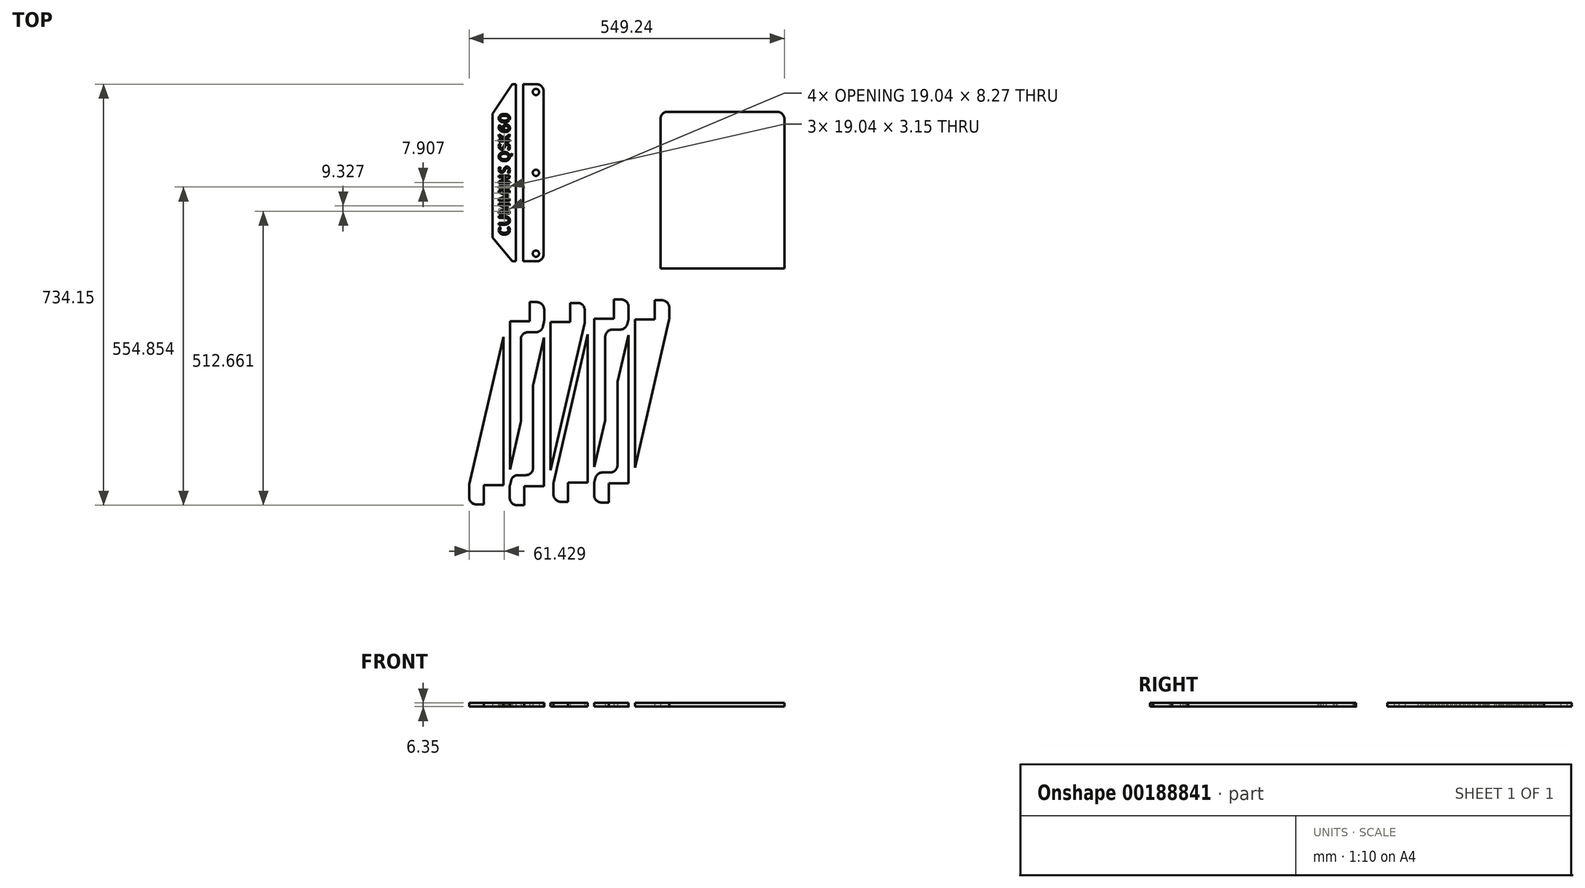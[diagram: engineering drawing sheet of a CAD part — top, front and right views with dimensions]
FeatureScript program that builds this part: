
annotation { "Feature Type Name" : "Feature", "Feature Type Description" : "" }
export const myFeature = defineFeature(function(context is Context, id is Id, definition is map)
    precondition{}
    {
        {
            var Q0;
            Q0=qCreatedBy(makeId("Top.planeOp"),FACE);
            var sketch = newSketch(context, id + "F0", { "sketchPlane" : qUnion([Q0])});
            skLineSegment(sketch, "E0.bottom", {"start": v(22.12, 104.51) * mm, "end": v(238.02, 104.51) * mm});
            skLineSegment(sketch, "E0.top", {"start": v(34.82, 377.56) * mm, "end": v(225.32, 377.56) * mm});
            skLineSegment(sketch, "E0.left", {"start": v(22.12, 104.51) * mm, "end": v(22.12, 364.86) * mm});
            skLineSegment(sketch, "E0.right", {"start": v(238.02, 104.51) * mm, "end": v(238.02, 364.86) * mm});
            skPoint(sketch, "E1.visualSharp", {"position": v(22.12, 377.56) * mm});
            skArc(sketch, "E1.filletArc", {"start": v(34.82, 377.56) * mm, "mid": v(25.83, 373.84) * mm, "end": v(22.12, 364.86) * mm});
            skPoint(sketch, "E2.visualSharp", {"position": v(238.02, 377.56) * mm});
            skArc(sketch, "E2.filletArc", {"start": v(238.02, 364.86) * mm, "mid": v(234.3, 373.84) * mm, "end": v(225.32, 377.56) * mm});
            skPoint(sketch, "E3", {"position": v(-194.8, 412.07) * mm});
            skPoint(sketch, "E4", {"position": v(-194.8, 271.07) * mm});
            skPoint(sketch, "E5", {"position": v(-194.8, 130.08) * mm});
            skLineSegment(sketch, "E6", {"start": v(-181.3, 129.3) * mm, "end": v(-181.3, 412.86) * mm});
            skLineSegment(sketch, "E7", {"start": v(-194, 116.6) * mm, "end": v(-216.87, 116.6) * mm});
            skLineSegment(sketch, "E8", {"start": v(-194, 425.56) * mm, "end": v(-216.87, 425.56) * mm});
            skPoint(sketch, "E9.visualSharp", {"position": v(-181.3, 116.6) * mm});
            skArc(sketch, "E9.filletArc", {"start": v(-194, 116.6) * mm, "mid": v(-185.03, 120.31) * mm, "end": v(-181.3, 129.3) * mm});
            skPoint(sketch, "E10.visualSharp", {"position": v(-181.3, 425.56) * mm});
            skArc(sketch, "E10.filletArc", {"start": v(-181.3, 412.86) * mm, "mid": v(-185.03, 421.84) * mm, "end": v(-194, 425.56) * mm});
            skLineSegment(sketch, "E11", {"start": v(-216.87, 116.6) * mm, "end": v(-216.87, 425.56) * mm});
            skLineSegment(sketch, "E12", {"start": v(-270.11, 158.02) * mm, "end": v(-270.11, 373.97) * mm});
            skLineSegment(sketch, "E13", {"start": v(-270.11, 373.97) * mm, "end": v(-235.82, 425.56) * mm});
            skLineSegment(sketch, "E14", {"start": v(-235.82, 425.56) * mm, "end": v(-229.47, 425.56) * mm});
            skLineSegment(sketch, "E15", {"start": v(-229.47, 425.56) * mm, "end": v(-229.47, 116.6) * mm});
            skLineSegment(sketch, "E16", {"start": v(-229.47, 116.6) * mm, "end": v(-235.82, 116.6) * mm});
            skLineSegment(sketch, "E17", {"start": v(-235.82, 116.6) * mm, "end": v(-270.11, 158.02) * mm});
            skText(sketch, "E18", { "text": "CUMMINS QSK60", "fontName": "AllertaStencil-Regular.ttf"});
            skLineSegment(sketch, "E19", {"start": v(-169.38, -247.72) * mm, "end": v(-110.01, 9.41) * mm});
            skLineSegment(sketch, "E20", {"start": v(-109.69, 12.27) * mm, "end": v(-109.69, 31.47) * mm});
            skLineSegment(sketch, "E21", {"start": v(-122.39, 44.17) * mm, "end": v(-135.09, 44.17) * mm});
            skLineSegment(sketch, "E22", {"start": v(-135.09, 44.17) * mm, "end": v(-135.09, 10.82) * mm});
            skLineSegment(sketch, "E23", {"start": v(-135.09, 10.82) * mm, "end": v(-169.38, 10.82) * mm});
            skLineSegment(sketch, "E24", {"start": v(-169.38, 10.82) * mm, "end": v(-169.38, -247.72) * mm});
            skPoint(sketch, "E25.visualSharp", {"position": v(-109.69, 44.17) * mm});
            skArc(sketch, "E25.filletArc", {"start": v(-109.69, 31.47) * mm, "mid": v(-113.4, 40.45) * mm, "end": v(-122.39, 44.17) * mm});
            skLineSegment(sketch, "E26", {"start": v(-180.48, 13.57) * mm, "end": v(-180.48, 32.77) * mm});
            skLineSegment(sketch, "E27", {"start": v(-193.18, 45.47) * mm, "end": v(-205.88, 45.47) * mm});
            skLineSegment(sketch, "E28", {"start": v(-205.88, 45.47) * mm, "end": v(-205.88, 12.12) * mm});
            skLineSegment(sketch, "E29", {"start": v(-205.88, 12.12) * mm, "end": v(-240.17, 12.12) * mm});
            skLineSegment(sketch, "E30", {"start": v(-240.17, 12.12) * mm, "end": v(-240.17, -246.42) * mm});
            skPoint(sketch, "E31.visualSharp", {"position": v(-180.48, 45.47) * mm});
            skArc(sketch, "E31.filletArc", {"start": v(-180.48, 32.77) * mm, "mid": v(-184.2, 41.75) * mm, "end": v(-193.18, 45.47) * mm});
            skPoint(sketch, "E32.visualSharp", {"position": v(-180.48, 12.12) * mm});
            skArc(sketch, "E32.filletArc", {"start": v(-180.8, 10.71) * mm, "mid": v(-180.56, 12.13) * mm, "end": v(-180.48, 13.57) * mm});
            skPoint(sketch, "E33.visualSharp", {"position": v(-109.69, 10.82) * mm});
            skArc(sketch, "E33.filletArc", {"start": v(-110.01, 9.41) * mm, "mid": v(-109.77, 10.83) * mm, "end": v(-109.69, 12.27) * mm});
            skLineSegment(sketch, "E34", {"start": v(-221.12, -19.63) * mm, "end": v(-221.12, -162.46) * mm});
            skLineSegment(sketch, "E35", {"start": v(-208.42, -6.93) * mm, "end": v(-194.98, -6.93) * mm});
            skLineSegment(sketch, "E36", {"start": v(-240.17, -246.42) * mm, "end": v(-221.45, -165.32) * mm});
            skLineSegment(sketch, "E37", {"start": v(-182.6, 2.92) * mm, "end": v(-180.8, 10.71) * mm});
            skPoint(sketch, "E38.visualSharp", {"position": v(-221.12, -163.9) * mm});
            skArc(sketch, "E38.filletArc", {"start": v(-221.45, -165.32) * mm, "mid": v(-221.2, -163.9) * mm, "end": v(-221.12, -162.46) * mm});
            skPoint(sketch, "E39.visualSharp", {"position": v(-184.88, -6.93) * mm});
            skArc(sketch, "E39.filletArc", {"start": v(-194.98, -6.93) * mm, "mid": v(-187.07, -4.16) * mm, "end": v(-182.6, 2.92) * mm});
            skPoint(sketch, "E40.visualSharp", {"position": v(-221.12, -6.93) * mm});
            skArc(sketch, "E40.filletArc", {"start": v(-208.42, -6.93) * mm, "mid": v(-217.4, -10.65) * mm, "end": v(-221.12, -19.63) * mm});
            skCircle(sketch, "E41", {"center": v(-194.8, 130.08) * mm, "radius": 5.5 * mm});
            skCircle(sketch, "E42", {"center": v(-194.8, 271.07) * mm, "radius": 5.5 * mm});
            skCircle(sketch, "E43", {"center": v(-194.8, 412.07) * mm, "radius": 5.5 * mm});
            skLineSegment(sketch, "E44", {"start": v(-22.32, -243.1) * mm, "end": v(37.04, 14.03) * mm});
            skLineSegment(sketch, "E45", {"start": v(37.37, 16.89) * mm, "end": v(37.37, 36.09) * mm});
            skLineSegment(sketch, "E46", {"start": v(24.67, 48.79) * mm, "end": v(11.97, 48.79) * mm});
            skLineSegment(sketch, "E47", {"start": v(11.97, 48.79) * mm, "end": v(11.97, 15.44) * mm});
            skLineSegment(sketch, "E48", {"start": v(11.97, 15.44) * mm, "end": v(-22.32, 15.44) * mm});
            skLineSegment(sketch, "E49", {"start": v(-22.32, 15.44) * mm, "end": v(-22.32, -243.1) * mm});
            skPoint(sketch, "E50.visualSharp", {"position": v(37.37, 48.79) * mm});
            skArc(sketch, "E50.filletArc", {"start": v(37.37, 36.09) * mm, "mid": v(33.65, 45.07) * mm, "end": v(24.67, 48.79) * mm});
            skLineSegment(sketch, "E51", {"start": v(-33.42, 18.19) * mm, "end": v(-33.42, 37.39) * mm});
            skLineSegment(sketch, "E52", {"start": v(-46.12, 50.09) * mm, "end": v(-58.82, 50.09) * mm});
            skLineSegment(sketch, "E53", {"start": v(-58.82, 50.09) * mm, "end": v(-58.82, 16.74) * mm});
            skLineSegment(sketch, "E54", {"start": v(-58.82, 16.74) * mm, "end": v(-93.11, 16.74) * mm});
            skLineSegment(sketch, "E55", {"start": v(-93.11, 16.74) * mm, "end": v(-93.11, -241.8) * mm});
            skPoint(sketch, "E56.visualSharp", {"position": v(-33.42, 50.09) * mm});
            skArc(sketch, "E56.filletArc", {"start": v(-33.42, 37.39) * mm, "mid": v(-37.14, 46.37) * mm, "end": v(-46.12, 50.09) * mm});
            skPoint(sketch, "E57.visualSharp", {"position": v(-33.42, 16.74) * mm});
            skArc(sketch, "E57.filletArc", {"start": v(-33.75, 15.33) * mm, "mid": v(-33.5, 16.75) * mm, "end": v(-33.42, 18.19) * mm});
            skPoint(sketch, "E58.visualSharp", {"position": v(37.37, 15.44) * mm});
            skArc(sketch, "E58.filletArc", {"start": v(37.04, 14.03) * mm, "mid": v(37.29, 15.45) * mm, "end": v(37.37, 16.89) * mm});
            skLineSegment(sketch, "E59", {"start": v(-74.06, -15.01) * mm, "end": v(-74.06, -157.84) * mm});
            skLineSegment(sketch, "E60", {"start": v(-61.36, -2.31) * mm, "end": v(-47.92, -2.31) * mm});
            skLineSegment(sketch, "E61", {"start": v(-93.11, -241.8) * mm, "end": v(-74.39, -160.7) * mm});
            skLineSegment(sketch, "E62", {"start": v(-35.55, 7.53) * mm, "end": v(-33.75, 15.33) * mm});
            skPoint(sketch, "E63.visualSharp", {"position": v(-74.06, -159.3) * mm});
            skArc(sketch, "E63.filletArc", {"start": v(-74.39, -160.7) * mm, "mid": v(-74.15, -159.28) * mm, "end": v(-74.06, -157.84) * mm});
            skPoint(sketch, "E64.visualSharp", {"position": v(-37.82, -2.31) * mm});
            skArc(sketch, "E64.filletArc", {"start": v(-47.92, -2.31) * mm, "mid": v(-40.02, 0.45) * mm, "end": v(-35.55, 7.53) * mm});
            skPoint(sketch, "E65.visualSharp", {"position": v(-74.06, -2.31) * mm});
            skArc(sketch, "E65.filletArc", {"start": v(-61.36, -2.31) * mm, "mid": v(-70.34, -6.03) * mm, "end": v(-74.06, -15.01) * mm});
            skLineSegment(sketch, "E66", {"start": v(-104.48, -10.78) * mm, "end": v(-163.84, -267.92) * mm});
            skLineSegment(sketch, "E67", {"start": v(-164.17, -270.77) * mm, "end": v(-164.17, -289.98) * mm});
            skLineSegment(sketch, "E68", {"start": v(-151.47, -302.68) * mm, "end": v(-138.77, -302.68) * mm});
            skLineSegment(sketch, "E69", {"start": v(-138.77, -302.68) * mm, "end": v(-138.77, -269.33) * mm});
            skLineSegment(sketch, "E70", {"start": v(-138.77, -269.33) * mm, "end": v(-104.48, -269.33) * mm});
            skLineSegment(sketch, "E71", {"start": v(-104.48, -269.33) * mm, "end": v(-104.48, -10.78) * mm});
            skPoint(sketch, "E72.visualSharp", {"position": v(-164.17, -302.68) * mm});
            skArc(sketch, "E72.filletArc", {"start": v(-164.17, -289.98) * mm, "mid": v(-160.45, -298.96) * mm, "end": v(-151.47, -302.68) * mm});
            skLineSegment(sketch, "E73", {"start": v(-93.38, -272.07) * mm, "end": v(-93.38, -291.28) * mm});
            skLineSegment(sketch, "E74", {"start": v(-80.68, -303.98) * mm, "end": v(-67.98, -303.98) * mm});
            skLineSegment(sketch, "E75", {"start": v(-67.98, -303.98) * mm, "end": v(-67.98, -270.63) * mm});
            skLineSegment(sketch, "E76", {"start": v(-67.98, -270.63) * mm, "end": v(-33.69, -270.63) * mm});
            skLineSegment(sketch, "E77", {"start": v(-33.69, -270.63) * mm, "end": v(-33.69, -12.08) * mm});
            skPoint(sketch, "E78.visualSharp", {"position": v(-93.38, -303.98) * mm});
            skArc(sketch, "E78.filletArc", {"start": v(-93.38, -291.28) * mm, "mid": v(-89.66, -300.26) * mm, "end": v(-80.68, -303.98) * mm});
            skPoint(sketch, "E79.visualSharp", {"position": v(-93.38, -270.63) * mm});
            skArc(sketch, "E79.filletArc", {"start": v(-93.05, -269.22) * mm, "mid": v(-93.3, -270.64) * mm, "end": v(-93.38, -272.07) * mm});
            skPoint(sketch, "E80.visualSharp", {"position": v(-164.17, -269.33) * mm});
            skArc(sketch, "E80.filletArc", {"start": v(-163.84, -267.92) * mm, "mid": v(-164.08, -269.34) * mm, "end": v(-164.17, -270.77) * mm});
            skLineSegment(sketch, "E81", {"start": v(-52.74, -238.88) * mm, "end": v(-52.74, -96.04) * mm});
            skLineSegment(sketch, "E82", {"start": v(-65.44, -251.58) * mm, "end": v(-78.87, -251.58) * mm});
            skLineSegment(sketch, "E83", {"start": v(-33.69, -12.08) * mm, "end": v(-52.4, -93.19) * mm});
            skLineSegment(sketch, "E84", {"start": v(-91.25, -261.42) * mm, "end": v(-93.05, -269.22) * mm});
            skPoint(sketch, "E85.visualSharp", {"position": v(-52.74, -94.6) * mm});
            skArc(sketch, "E85.filletArc", {"start": v(-52.4, -93.19) * mm, "mid": v(-52.65, -94.6) * mm, "end": v(-52.74, -96.04) * mm});
            skPoint(sketch, "E86.visualSharp", {"position": v(-88.98, -251.58) * mm});
            skArc(sketch, "E86.filletArc", {"start": v(-78.87, -251.58) * mm, "mid": v(-86.78, -254.34) * mm, "end": v(-91.25, -261.42) * mm});
            skPoint(sketch, "E87.visualSharp", {"position": v(-52.74, -251.58) * mm});
            skArc(sketch, "E87.filletArc", {"start": v(-65.44, -251.58) * mm, "mid": v(-56.45, -247.86) * mm, "end": v(-52.74, -238.88) * mm});
            skLineSegment(sketch, "E88", {"start": v(-251.53, -15.4) * mm, "end": v(-310.9, -272.53) * mm});
            skLineSegment(sketch, "E89", {"start": v(-311.22, -275.39) * mm, "end": v(-311.22, -294.6) * mm});
            skLineSegment(sketch, "E90", {"start": v(-298.52, -307.3) * mm, "end": v(-285.82, -307.3) * mm});
            skLineSegment(sketch, "E91", {"start": v(-285.82, -307.3) * mm, "end": v(-285.82, -273.94) * mm});
            skLineSegment(sketch, "E92", {"start": v(-285.82, -273.94) * mm, "end": v(-251.53, -273.94) * mm});
            skLineSegment(sketch, "E93", {"start": v(-251.53, -273.94) * mm, "end": v(-251.53, -15.4) * mm});
            skPoint(sketch, "E94.visualSharp", {"position": v(-311.22, -307.3) * mm});
            skArc(sketch, "E94.filletArc", {"start": v(-311.22, -294.6) * mm, "mid": v(-307.5, -303.57) * mm, "end": v(-298.52, -307.3) * mm});
            skLineSegment(sketch, "E95", {"start": v(-240.43, -276.69) * mm, "end": v(-240.43, -295.9) * mm});
            skLineSegment(sketch, "E96", {"start": v(-227.73, -308.6) * mm, "end": v(-215.03, -308.6) * mm});
            skLineSegment(sketch, "E97", {"start": v(-215.03, -308.6) * mm, "end": v(-215.03, -275.24) * mm});
            skLineSegment(sketch, "E98", {"start": v(-215.03, -275.24) * mm, "end": v(-180.74, -275.24) * mm});
            skLineSegment(sketch, "E99", {"start": v(-180.74, -275.24) * mm, "end": v(-180.74, -16.7) * mm});
            skPoint(sketch, "E100.visualSharp", {"position": v(-240.43, -308.6) * mm});
            skArc(sketch, "E100.filletArc", {"start": v(-240.43, -295.9) * mm, "mid": v(-236.71, -304.87) * mm, "end": v(-227.73, -308.6) * mm});
            skPoint(sketch, "E101.visualSharp", {"position": v(-240.43, -275.24) * mm});
            skArc(sketch, "E101.filletArc", {"start": v(-240.1, -273.83) * mm, "mid": v(-240.35, -275.25) * mm, "end": v(-240.43, -276.69) * mm});
            skPoint(sketch, "E102.visualSharp", {"position": v(-311.22, -273.94) * mm});
            skArc(sketch, "E102.filletArc", {"start": v(-310.9, -272.53) * mm, "mid": v(-311.14, -273.95) * mm, "end": v(-311.22, -275.39) * mm});
            skLineSegment(sketch, "E103", {"start": v(-199.8, -243.5) * mm, "end": v(-199.8, -100.66) * mm});
            skLineSegment(sketch, "E104", {"start": v(-212.5, -256.2) * mm, "end": v(-225.93, -256.2) * mm});
            skLineSegment(sketch, "E105", {"start": v(-180.74, -16.7) * mm, "end": v(-199.47, -97.8) * mm});
            skLineSegment(sketch, "E106", {"start": v(-238.3, -266.03) * mm, "end": v(-240.1, -273.83) * mm});
            skPoint(sketch, "E107.visualSharp", {"position": v(-199.8, -99.21) * mm});
            skArc(sketch, "E107.filletArc", {"start": v(-199.47, -97.8) * mm, "mid": v(-199.71, -99.22) * mm, "end": v(-199.8, -100.66) * mm});
            skPoint(sketch, "E108.visualSharp", {"position": v(-236.03, -256.2) * mm});
            skArc(sketch, "E108.filletArc", {"start": v(-225.93, -256.2) * mm, "mid": v(-233.84, -258.95) * mm, "end": v(-238.3, -266.03) * mm});
            skPoint(sketch, "E109.visualSharp", {"position": v(-199.8, -256.2) * mm});
            skArc(sketch, "E109.filletArc", {"start": v(-212.5, -256.2) * mm, "mid": v(-203.51, -252.47) * mm, "end": v(-199.8, -243.5) * mm});
            const initialGuessF0  = {"E18": [-0.24027, 0.16118, 0, 1, 0.01905]};
            skSetInitialGuess(sketch, initialGuessF0);
            skSolve(sketch);
        }
        {
            var Q0;
            Q0=makeQuery(id+"F0.imprint","IMPRINT",FACE,{"disambiguationData":[TD([[makeQuery(id+"F0.imprint","IMPRINT",EDGE,{"derivedFrom":sQuery(id+"F0.wireOp",EDGE,"E12")}),-1.0]])]});
            var Q1;
            Q1=makeQuery(id+"F0.imprint","IMPRINT",FACE,{"disambiguationData":[TD([[makeQuery(id+"F0.imprint","IMPRINT",EDGE,{"derivedFrom":sQuery(id+"F0.wireOp",EDGE,"E6")}),1.0]])]});
            var Q2;
            Q2=makeQuery(id+"F0.imprint","IMPRINT",FACE,{"disambiguationData":[TD([[makeQuery(id+"F0.imprint","IMPRINT",EDGE,{"derivedFrom":sQuery(id+"F0.wireOp",EDGE,"E0.top")}),-1.0]])]});
            var Q3;
            Q3=makeQuery(id+"F0.imprint","IMPRINT",FACE,{"disambiguationData":[TD([[makeQuery(id+"F0.imprint","IMPRINT",EDGE,{"derivedFrom":sQuery(id+"F0.wireOp",EDGE,"E44")}),1.0]])]});
            var Q4;
            Q4=makeQuery(id+"F0.imprint","IMPRINT",FACE,{"disambiguationData":[TD([[makeQuery(id+"F0.imprint","IMPRINT",EDGE,{"derivedFrom":sQuery(id+"F0.wireOp",EDGE,"E51")}),1.0]])]});
            var Q5;
            Q5=makeQuery(id+"F0.imprint","IMPRINT",FACE,{"disambiguationData":[TD([[makeQuery(id+"F0.imprint","IMPRINT",EDGE,{"derivedFrom":sQuery(id+"F0.wireOp",EDGE,"E19")}),1.0]])]});
            var Q6;
            Q6=makeQuery(id+"F0.imprint","IMPRINT",FACE,{"disambiguationData":[TD([[makeQuery(id+"F0.imprint","IMPRINT",EDGE,{"derivedFrom":sQuery(id+"F0.wireOp",EDGE,"E26")}),1.0]])]});
            var Q7;
            Q7=makeQuery(id+"F0.imprint","IMPRINT",FACE,{"disambiguationData":[TD([[makeQuery(id+"F0.imprint","IMPRINT",EDGE,{"derivedFrom":sQuery(id+"F0.wireOp",EDGE,"E88")}),1.0]])]});
            var Q8;
            Q8=makeQuery(id+"F0.imprint","IMPRINT",FACE,{"disambiguationData":[TD([[makeQuery(id+"F0.imprint","IMPRINT",EDGE,{"derivedFrom":sQuery(id+"F0.wireOp",EDGE,"E95")}),1.0]])]});
            var Q9;
            Q9=makeQuery(id+"F0.imprint","IMPRINT",FACE,{"disambiguationData":[TD([[makeQuery(id+"F0.imprint","IMPRINT",EDGE,{"derivedFrom":sQuery(id+"F0.wireOp",EDGE,"E66")}),1.0]])]});
            var Q10;
            Q10=makeQuery(id+"F0.imprint","IMPRINT",FACE,{"disambiguationData":[TD([[makeQuery(id+"F0.imprint","IMPRINT",EDGE,{"derivedFrom":sQuery(id+"F0.wireOp",EDGE,"E73")}),1.0]])]});
            extrude(context, id + "F1", {"entities" : qUnion([Q0, Q1, Q2, Q3, Q4, Q5, Q6, Q7, Q8, Q9, Q10]), "depth" : 6.35 * mm});
        }
    });
